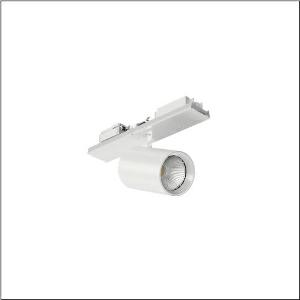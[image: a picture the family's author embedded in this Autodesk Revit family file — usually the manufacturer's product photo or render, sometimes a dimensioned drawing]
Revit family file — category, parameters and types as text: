
# Revit family: licross_r__spot_31_51sl12da43b_285d
name_source: partatom
category: Lighting Fixtures
units: mm (PartAtom-declared; Revit-internal decimal feet)

## family parameters
Cut with Voids When Loaded = No
Host = Face
Light Source = No
Part Type = Normal
Room Calculation Point = No
Round Connector Dimension = Use Diameter
Shared = No

## types (1)
- --- (1 x LED, 3650 lm, 28.6 W, 4000K)
    Apparent Load = 29 VA
    CIE Flux Codes = 93 97 99 100 100
    Color Rendering = 90
    Color Temperature = 4000K
    Default Elevation = 1800 mm
    Description = Licross® Spot 31, directional spotlight, light control with lens, of plastic, LED rated luminous flux: 3.650lm, light colour: 940, with plug, 5-pole, mains connection: 220..240V, AC, 50/60Hz, of aluminium, traffic white (RAL 9016), length: 140mm, diameter: 90mm, protection rating (complete): IP20, insulation class (complete): insulation class I (protective earthing), certification: CE, packaging unit: 1 piece
    Height = 175 mm
    Lamp = 1 x LED
    Lamp Light Flux = 3650 lm
    Lamp Power = 28.6 W
    Lamp count = 1
    Length = 90 mm
    Luminous efficacy = 128 lm/W
    Manufacturer = Siteco
    ModVariant = No
    Model = 51SL12DA43B
    Mounting Place = Ceiling
    Mounting Type = Pendant
    Number of Poles = 1
    OnlyDefault = Yes
    Power Factor = 1
    Product Name = Licross® Spot 31
    Product group = directional spotlight
    ProductGroupID = 905
    Protection Class = Protection class I
    Protection Degree = IP 20
    RLX_Detail_Level = 1
    RLX_Emergency_Light_Flux = 0 lm
    RLX_Emergency_Type = 0
    RLX_Emergency_Type_DB = No
    RlxData = <blob elided: 14777 chars, md5=98f126d6>
    Socket = socket
    Standby Power = 0 W
    System Light Flux = 3650 lm
    System Power = 29 W
    Type Comments = factory setting: luminous flux: 100 % | (ON | ON | ON) | 700 mA
    Type Image = l_1245720.jpg
    URL = http://relux.com
    VarID = @adj_064023
    Voltage = 0 V
    Weight = 0.00 kg
    Width = 0 mm  [stored 0 ft]

note: [stored X ft] marks values corroborated as IEEE doubles in the binary element streams (Revit-internal decimal feet)

## geometry (parser evidence)
native form markers: Sweep x11
no freeform markers — native parametric forms only
